# Revit family: LOROWERK 21516-125X
name_source: partatom
category: Sanitärinstallationen
revit_build: Autodesk Revit 2017 (Build: 20160225_1515(x64)
units: mm (PartAtom-declared; Revit-internal decimal feet)

## family parameters
Arbeitsebenenbasiert = Nein
Beim Laden mit Abzugskörper schneiden = Nein
Bemaßung runder Anschluss = Durchmesser verwenden
Gemeinsam genutzt = Nein
Immer vertikal = Ja
Raumberechnungspunkt = Nein
Teiletyp = Normal

## types (1)
- LOROWERK 21516-125X
    38.710.01.13 = seitlich
    38.710.01.5 = DN
    Abdichtvarianten = mit Klemmflansch
    Abflussstutzen Ausführung = waagerecht
    Ablaufanschluss = 1
    Art der Nenn-/Betriebsspannung = nicht zutreffend
    BIM = https://media.stage.bim.site
    Beschreibung = LORO-DRAINLET DL Flachdachabläufe, Kompletteinheiten, einteilig
    Bestellmenge (Multiplikator) = 1
    CONNECTOR0_DIAMETER_dZ_0r = 125 mm
    CONNECTOR0_dZ_00 = 11 mm
    CONNECTOR0_dZ_01 = 12 mm  [stored 0.0393701 ft]
    CONNECTOR0_ref_dZ = 12 mm  [stored 0.0393701 ft]
    CONNECTOR1_DIAMETER_dNBN0_0r = 125 mm
    CONNECTOR1_dNBN0_00 = 46 mm
    CONNECTOR1_dNBN0_01 = 291 mm
    CONNECTOR1_ref_dNBN0 = 46 mm
    CONNECTOR1_ref_dNBN1 = 108 mm
    DATANORM = 21516.125X
    Einbaubreite [m] = 0.322
    Einbautiefe [m] = 0.035
    Feuerwiderstandsklasse = keine Feuerwiderstandsklasse
    Feuerwiderstandsklasse nachrüstbar = nein
    GTIN = 4038088085875
    Gehäuseanschlussarten = Ablauf punktförmig
    Geruchsverschluss = ohne Geruchsverschluss
    HAN = 21516.125X
    Heizung = mit Heizung
    Hersteller = LOROWERK K.H. Vahlbrauk GmbH & Co. KG
    Ist System = Nein
    Ist Zubehör = Nein
    Kommentar = Kompletteinheit Serie 84 einteilig
    Nenndruck = 453
    Nenndrucksystem = 330
    Nennweitensystem = PN
    Potenzialausgleich (Erdungsanschluss)   vorhanden = ja
    Produktbezeichnung = LORO-DL Ablauf, Edelstahl, Klemmflansch, seitl., 1-tlg., WD u. Heizung, DN125
    Produktklassifikation = Flachdachablauf
    Produktname = LORO-DL Ablauf, Edelstahl, Klemmflansch, seitl., 1-tlg., WD u. Heizung, DN125
    Produktvideo = https://media.stage.bim.site
    Sperrwasserhöhe [m] = 0
    Typname = LORO-DL Ablauf, Edelstahl, Klemmflansch, seitl., 1-tlg., WD u. Heizung, DN125
    VDIBSN = 0020030000020010000010010020010000000030020000002100000001
    Werkstoff des Ablaufkörpers = nicht rostender Stahl
    Wärmedämmung = mit Wärmedämmung
    elektrischer Anschluss = nein

note: [stored X ft] marks values corroborated as IEEE doubles in the binary element streams (Revit-internal decimal feet)
